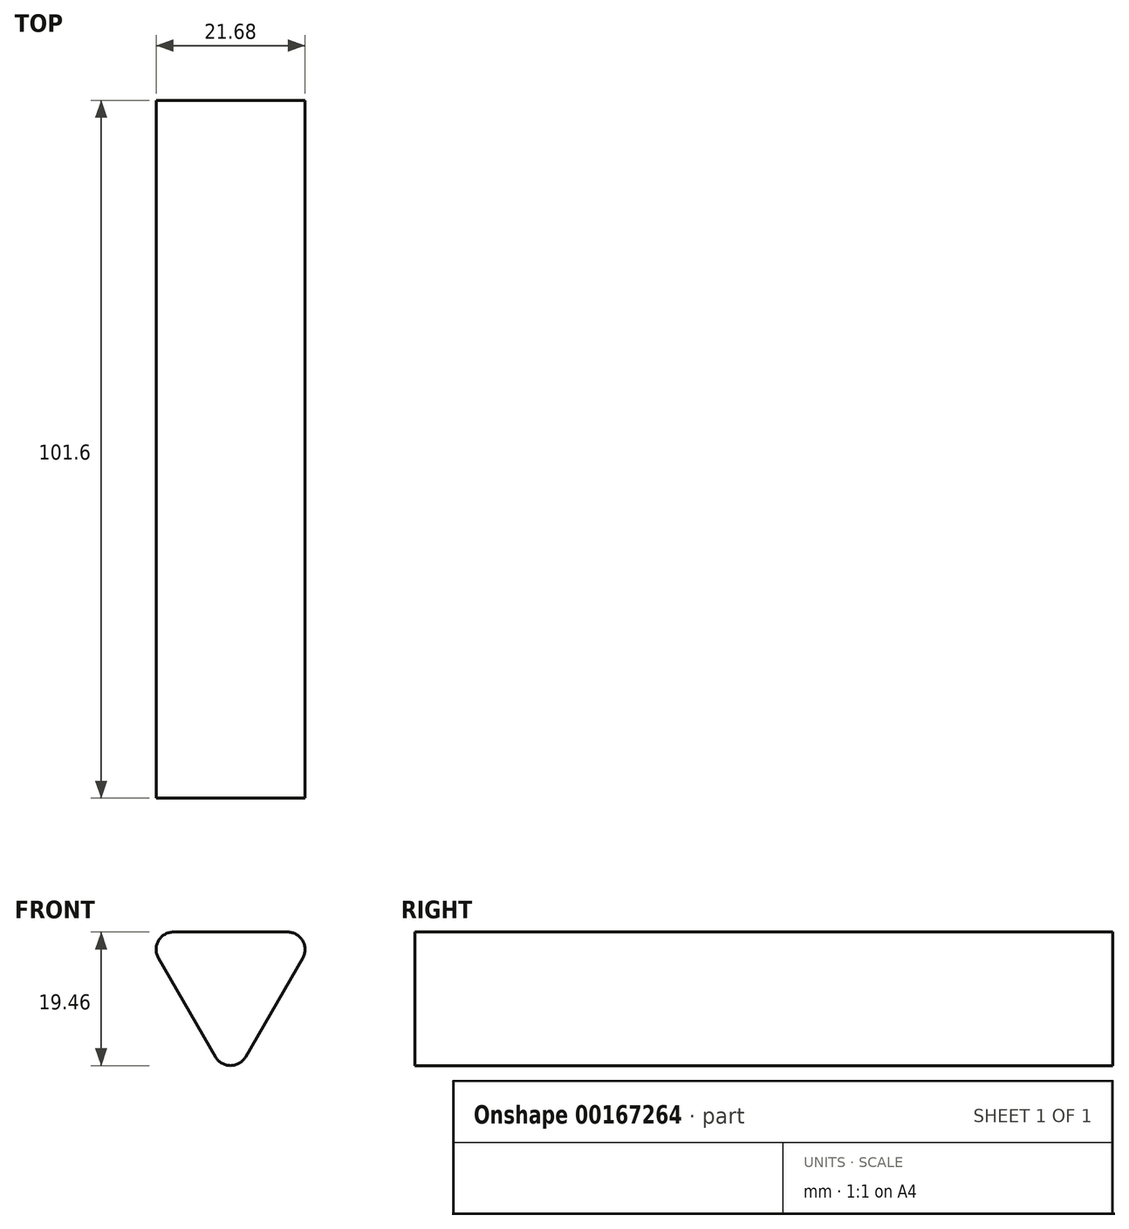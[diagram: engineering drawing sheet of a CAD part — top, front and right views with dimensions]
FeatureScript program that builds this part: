
annotation { "Feature Type Name" : "Feature", "Feature Type Description" : "" }
export const myFeature = defineFeature(function(context is Context, id is Id, definition is map)
    precondition{}
    {
        {
            var Q0;
            Q0=qCreatedBy(makeId("Front.planeOp"),FACE);
            var sketch = newSketch(context, id + "F0", { "sketchPlane" : qUnion([Q0])});
            skLineSegment(sketch, "E0", {"start": v(-10.5, 7.19) * mm, "end": v(-2.2, -7.19) * mm});
            skLineSegment(sketch, "E1", {"start": v(2.2, -7.19) * mm, "end": v(10.5, 7.19) * mm});
            skLineSegment(sketch, "E2", {"start": v(8.3, 11) * mm, "end": v(-8.3, 11) * mm});
            skLineSegment(sketch, "E3", {"start": v(-12.7, 11) * mm, "end": v(6.35, 0) * mm, "construction": true});
            skLineSegment(sketch, "E4", {"start": v(12.7, 11) * mm, "end": v(-6.35, 0) * mm, "construction": true});
            skLineSegment(sketch, "E5", {"start": v(0, -11) * mm, "end": v(0, 11) * mm, "construction": true});
            skPoint(sketch, "E6.visualSharp", {"position": v(-12.7, 11) * mm});
            skArc(sketch, "E6.filletArc", {"start": v(-8.3, 11) * mm, "mid": v(-10.5, 9.73) * mm, "end": v(-10.5, 7.19) * mm});
            skPoint(sketch, "E7.visualSharp", {"position": v(12.7, 11) * mm});
            skArc(sketch, "E7.filletArc", {"start": v(10.5, 7.19) * mm, "mid": v(10.5, 9.73) * mm, "end": v(8.3, 11) * mm});
            skPoint(sketch, "E8.visualSharp", {"position": v(0, -11) * mm});
            skArc(sketch, "E8.filletArc", {"start": v(-2.2, -7.19) * mm, "mid": v(0, -8.46) * mm, "end": v(2.2, -7.19) * mm});
            skSolve(sketch);
        }
        {
            var Q0;
            Q0=makeQuery(id+"F0.imprint","IMPRINT",FACE,{"disambiguationData":[TD([[makeQuery(id+"F0.imprint","IMPRINT",EDGE,{"derivedFrom":sQuery(id+"F0.wireOp",EDGE,"E0")}),1.0]])]});
            extrude(context, id + "F1", {"entities" : qUnion([Q0]), "depth" : 101.6 * mm});
        }
    });
